# Revit family: Lighting_Fixture-Ceiling-Astro-Taketa II
name_source: partatom
category: Lighting Fixtures
revit_build: Autodesk Revit 2018 (Build: 20170223_1515(x64)
units: mm (PartAtom-declared; Revit-internal decimal feet)

## family parameters
Cut with Voids When Loaded = No
Host = Face
Light Source = Yes
OmniClass Number = 23.80.70.11.11
OmniClass Title = General Luminaries, Non Directional
Part Type = Normal
Room Calculation Point = No
Round Connector Dimension = Use Diameter
Shared = No

## types (3) — shared parameters
Apparent Load = 30 VA
Assembly Code = D5020200
Class = 2
Color Filter = 16777215
Default Elevation = 1219.2 mm  [stored 4 ft]
Description = Ceiling Light
Diffuser Width = 280 mm  [stored 0.918635 ft]
Dimmable = No
Dimming Lamp Color Temperature Shift = <None>
Emit Shape Visible in Rendering = No
Emit from Rectangle Length = 280 mm  [stored 0.918635 ft]
Emit from Rectangle Width = 280 mm  [stored 0.918635 ft]
Energy Efficiency Rating = -
Height = 75 mm
IP Rating = IP44
Lamp included = Yes
Length = 300 mm  [stored 0.984252 ft]
Light Source Elevation = 60 mm  [stored 0.19685 ft]
Luminaire Lamp Efficiency Rating = -
Manufacturer = Astro Lighting Ltd, CM20 2DP
Mountable on normally flammable surfaces = Yes
Number of Poles = 1
Suitable for bathroom zone = zone 2, 3
Tilt Angle = -90.00°
URL = www.astrolighting.co.uk
Voltage = 230 V
Wall Bracket Material = Astro - Steel - Silver Paint
Wall Bracket Width = 228 mm  [stored 0.748031 ft]
Width = 300 mm  [stored 0.984252 ft]

## per-type parameters (varying)
| type | Casing Material | Lamp | Model | Photometric Web File | Product Documentation | Type Comments | Wattage Comments | Weight |
| 7159 Taketa LED (Chrome) | Astro - Aluminium - Chrome Finish | LED | 7159 Taketa LED | TRN-18318  Taketa LED II 7932 .ies | http://www.astrolighting.co.uk
/kw/7159/7159_Taketa-LED | Can be mounted on ceiling or wall
Includes integral LED driver | 17.7W | 3.0 kg |
| 0933 Taketa Plus (Chrome) | Astro - Aluminium - Chrome Finish | 4 pin 2D | 0933 Taketa Plus Chrome | 0933 TAKETA PLUS CHROME.ies | http://www.astrolighting.co.uk
/kw/0933/0933_Taketa-Plus | - Can be mounted on ceiling or wall - Includes integral electronic ballast | 28W | 3.3 kg |
| 0934 Taketa Plus (Matt Nickel) | Astro - Aluminium - Matt Nickel | 4 pin 2D | 0934 Taketa Plus Matt Nickel | 0933 TAKETA PLUS CHROME.ies | http://www.astrolighting.co.uk
/kw/0933/0933_Taketa-Plus | - Can be mounted on ceiling or wall - Includes integral electronic ballast | 28W | 3.3 kg |

note: [stored X ft] marks values corroborated as IEEE doubles in the binary element streams (Revit-internal decimal feet)

## geometry (parser evidence)
native form markers: Sweep x2
no freeform markers — native parametric forms only
